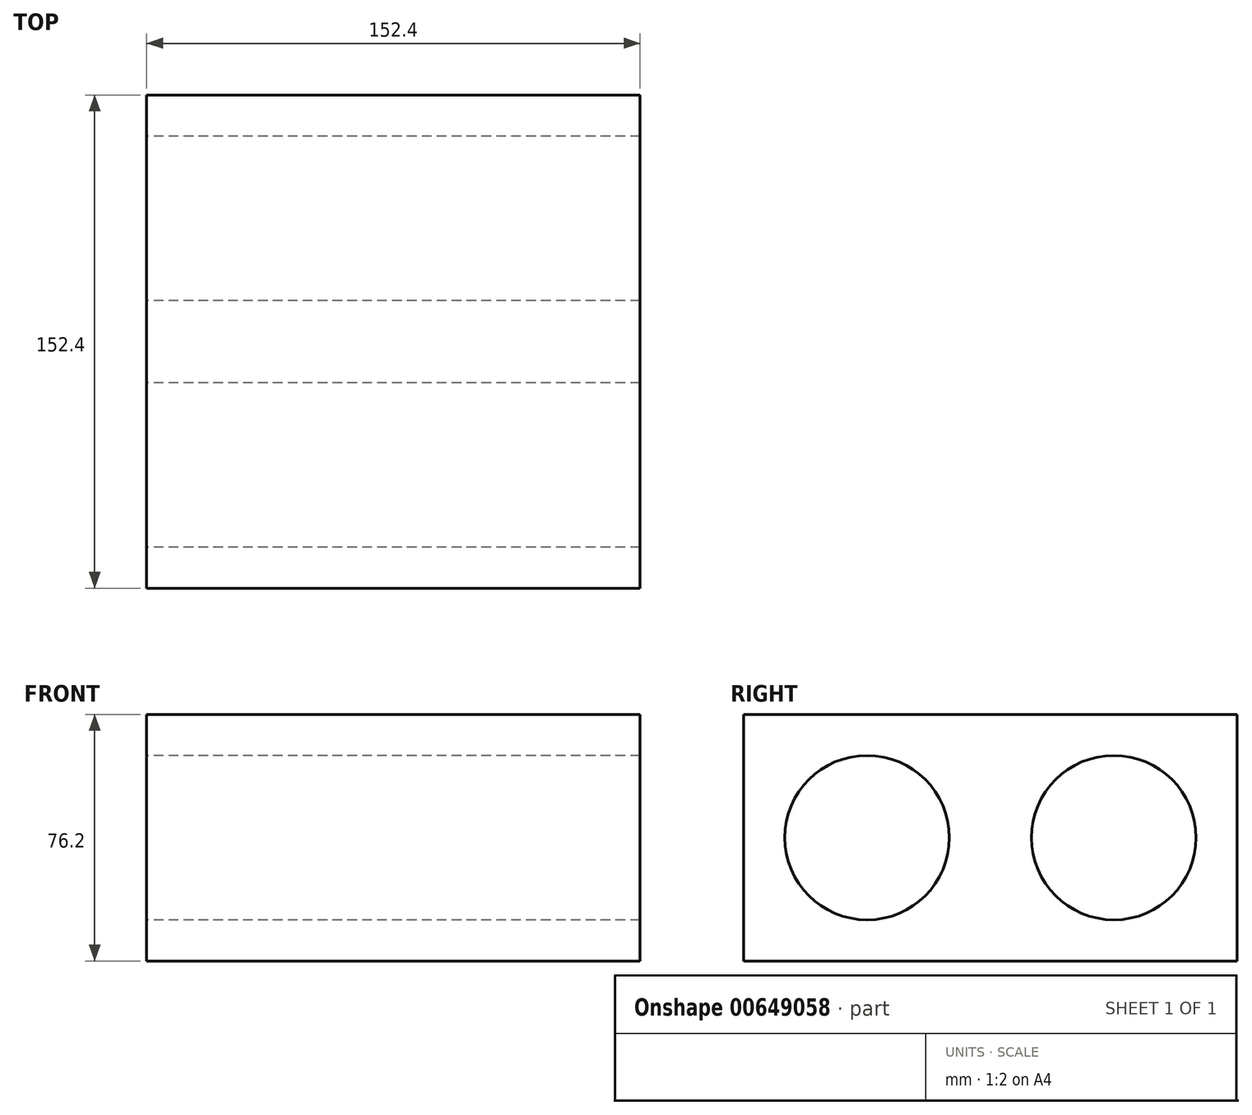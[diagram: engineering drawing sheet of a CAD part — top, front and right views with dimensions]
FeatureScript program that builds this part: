
annotation { "Feature Type Name" : "Feature", "Feature Type Description" : "" }
export const myFeature = defineFeature(function(context is Context, id is Id, definition is map)
    precondition{}
    {
        {
            var Q0;
            Q0=qCreatedBy(makeId("Right.planeOp"),FACE);
            var sketch = newSketch(context, id + "F0", { "sketchPlane" : qUnion([Q0])});
            skLineSegment(sketch, "E0.bottom", {"start": v(-66.6, 80.57) * mm, "end": v(85.8, 80.57) * mm});
            skLineSegment(sketch, "E0.top", {"start": v(-66.6, 4.37) * mm, "end": v(85.8, 4.37) * mm});
            skLineSegment(sketch, "E0.left", {"start": v(-66.6, 80.57) * mm, "end": v(-66.6, 4.37) * mm});
            skLineSegment(sketch, "E0.right", {"start": v(85.8, 80.57) * mm, "end": v(85.8, 4.37) * mm});
            skCircle(sketch, "E1", {"center": v(-28.5, 42.47) * mm, "radius": 25.4 * mm});
            skCircle(sketch, "E2", {"center": v(47.7, 42.47) * mm, "radius": 25.4 * mm});
            skSolve(sketch);
        }
        {
            var Q0;
            Q0=makeQuery(id+"F0.imprint","IMPRINT",FACE,{"disambiguationData":[TD([[makeQuery(id+"F0.imprint","IMPRINT",EDGE,{"derivedFrom":sQuery(id+"F0.wireOp",EDGE,"E0.bottom")}),-1.0]])]});
            extrude(context, id + "F1", {"entities" : qUnion([Q0]), "depth" : 152.4 * mm, "offsetDistance" : 25.4 * mm});
        }
    });
